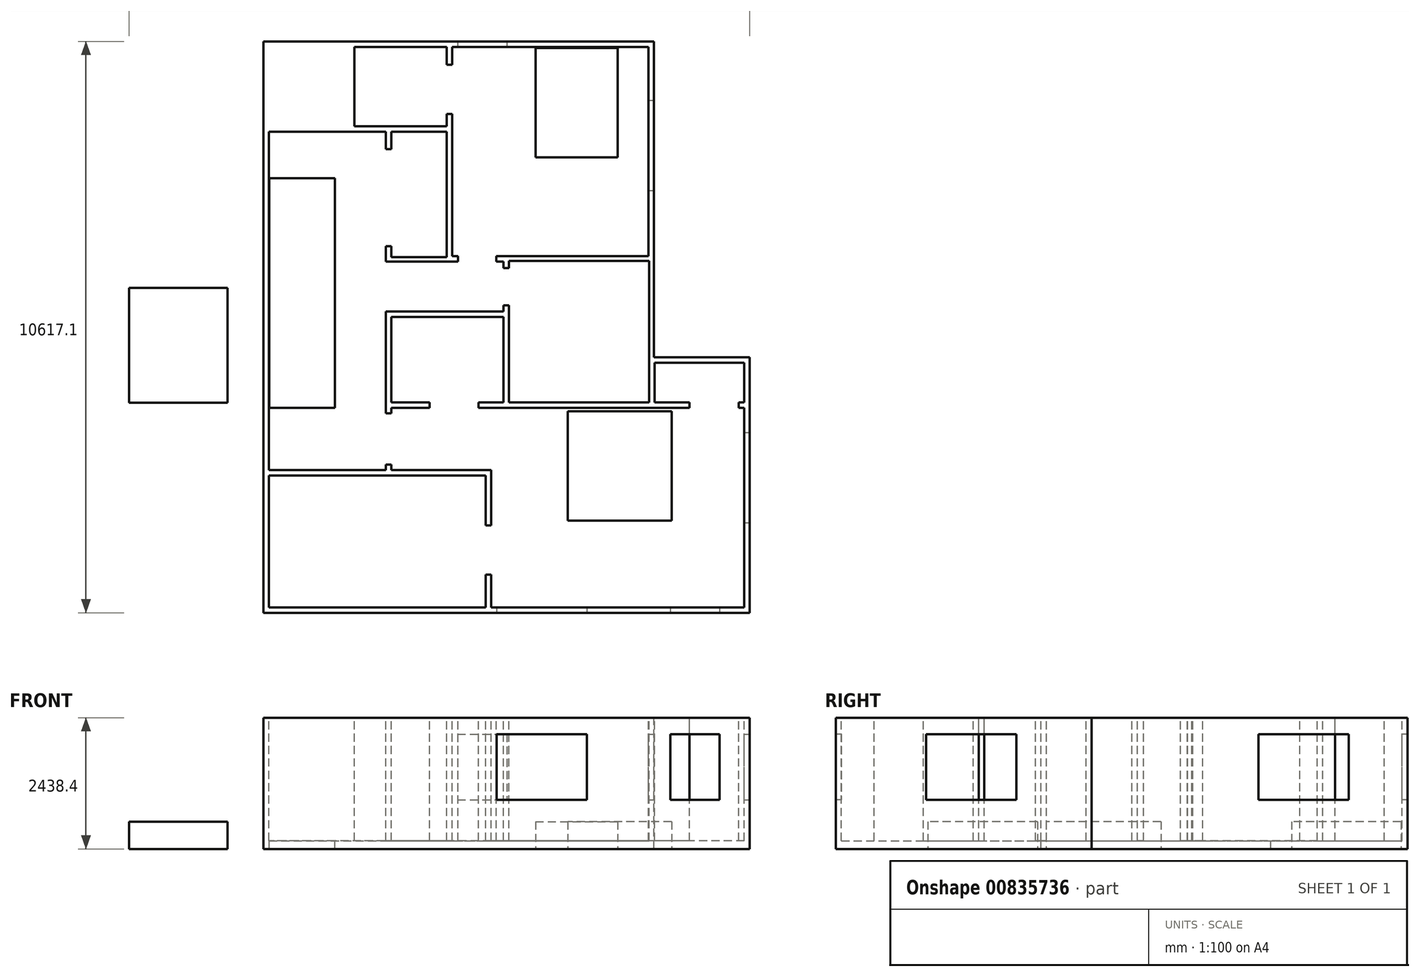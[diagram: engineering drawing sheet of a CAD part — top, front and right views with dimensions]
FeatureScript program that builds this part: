
annotation { "Feature Type Name" : "Feature", "Feature Type Description" : "" }
export const myFeature = defineFeature(function(context is Context, id is Id, definition is map)
    precondition{}
    {
        {
            var Q0;
            Q0=qCreatedBy(makeId("Top.planeOp"),FACE);
            var sketch = newSketch(context, id + "F0", { "sketchPlane" : qUnion([Q0])});
            skLineSegment(sketch, "E0.bottom", {"start": v(-4514.85, 5308.55) * mm, "end": v(4514.85, 5308.55) * mm});
            skLineSegment(sketch, "E0.top", {"start": v(-4514.85, -5308.55) * mm, "end": v(4514.85, -5308.55) * mm});
            skLineSegment(sketch, "E0.left", {"start": v(-4514.85, 5308.55) * mm, "end": v(-4514.85, -5308.55) * mm});
            skLineSegment(sketch, "E0.right", {"start": v(4514.85, 5308.55) * mm, "end": v(4514.85, -5308.55) * mm});
            skPoint(sketch, "E0.middle", {"position": v(0, 0) * mm});
            skSolve(sketch);
        }
        {
            var Q0;
            Q0 = qSketchRegion(id + "F0", true);
            extrude(context, id + "F1", {"entities" : qUnion([Q0]), "depth" : 2438.4 * mm, "offsetDistance" : 30.48 * mm});
        }
        {
            var Q0;
            Q0=makeQuery(id+"F1.opExtrude","CAP_FACE",FACE,{"disambiguationData":[OSD([sQuery(id+"F0.wireOp",EDGE,"E0.bottom"),sQuery(id+"F0.wireOp",EDGE,"E0.top"),sQuery(id+"F0.wireOp",EDGE,"E0.left"),sQuery(id+"F0.wireOp",EDGE,"E0.right")])],"isStart":false});
            var sketch = newSketch(context, id + "F2", { "sketchPlane" : qUnion([Q0])});
            skLineSegment(sketch, "E1.bottom", {"start": v(2736.95, 5308.55) * mm, "end": v(4514.85, 5308.55) * mm});
            skLineSegment(sketch, "E1.top", {"start": v(2736.95, -558.85) * mm, "end": v(4514.85, -558.85) * mm});
            skLineSegment(sketch, "E1.left", {"start": v(2736.95, 5308.55) * mm, "end": v(2736.95, -558.85) * mm});
            skLineSegment(sketch, "E1.right", {"start": v(4514.85, 5308.55) * mm, "end": v(4514.85, -558.85) * mm});
            skSolve(sketch);
        }
        {
            var Q0;
            Q0=makeQuery(id+"F2.imprint","IMPRINT",FACE,{"disambiguationData":[TD([[makeQuery(id+"F2.imprint","IMPRINT",EDGE,{"derivedFrom":sQuery(id+"F2.wireOp",EDGE,"E1.bottom")}),-1.0]])]});
            extrude(context, id + "F3", {"entities" : qUnion([Q0]), "operationType" : NewBodyOperationType.REMOVE, "oppositeDirection" : true, "depth" : 3048 * mm, "offsetDistance" : 30.48 * mm});
        }
        {
            var Q0;
            Q0=makeQuery(id+"F1.opExtrude","CAP_FACE",FACE,{"disambiguationData":[OSD([sQuery(id+"F0.wireOp",EDGE,"E0.bottom"),sQuery(id+"F0.wireOp",EDGE,"E0.top"),sQuery(id+"F0.wireOp",EDGE,"E0.left"),sQuery(id+"F0.wireOp",EDGE,"E0.right")])],"isStart":false});
            var sketch = newSketch(context, id + "F4", { "sketchPlane" : qUnion([Q0])});
            skLineSegment(sketch, "E2.bottom", {"start": v(4413.35, -5207.05) * mm, "end": v(-285.66, -5207.05) * mm});
            skLineSegment(sketch, "E2.top", {"start": v(4413.35, -1498.55) * mm, "end": v(4311.85, -1498.55) * mm});
            skLineSegment(sketch, "E2.left", {"start": v(4413.35, -5207.05) * mm, "end": v(4413.35, -3784.55) * mm});
            skLineSegment(sketch, "E2.right", {"start": v(-285.66, -5207.05) * mm, "end": v(-285.66, -4597.45) * mm});
            skLineSegment(sketch, "E3.bottom", {"start": v(-285.66, -1498.55) * mm, "end": v(-518.82, -1498.55) * mm});
            skLineSegment(sketch, "E3.right", {"start": v(-2144.32, -1498.55) * mm, "end": v(-2144.32, -1600.05) * mm});
            skLineSegment(sketch, "E4.bottom", {"start": v(-4413.35, -5207.05) * mm, "end": v(-387.16, -5207.05) * mm});
            skLineSegment(sketch, "E4.top", {"start": v(-4413.35, -2755.85) * mm, "end": v(-387.16, -2755.85) * mm});
            skLineSegment(sketch, "E4.left", {"start": v(-4413.35, -5207.05) * mm, "end": v(-4413.35, -2755.85) * mm});
            skLineSegment(sketch, "E4.right", {"start": v(-387.16, -5207.05) * mm, "end": v(-387.16, -4597.45) * mm});
            skLineSegment(sketch, "E5", {"start": v(-387.16, -4597.45) * mm, "end": v(-285.66, -4597.45) * mm});
            skLineSegment(sketch, "E6", {"start": v(-387.16, -3683.05) * mm, "end": v(-285.66, -3683.05) * mm});
            skLineSegment(sketch, "E7.trimOffspring", {"start": v(-387.16, -3683.05) * mm, "end": v(-387.16, -2755.85) * mm});
            skLineSegment(sketch, "E8.trimOffspring", {"start": v(4413.35, -2108.15) * mm, "end": v(4413.35, -1498.55) * mm});
            skLineSegment(sketch, "E9", {"start": v(4413.35, -3784.55) * mm, "end": v(4413.35, -2108.15) * mm});
            skLineSegment(sketch, "E10.bottom", {"start": v(-2144.32, -1397.05) * mm, "end": v(-1433.22, -1397.05) * mm});
            skLineSegment(sketch, "E10.top", {"start": v(-2144.32, 190.35) * mm, "end": v(-61.62, 190.35) * mm});
            skLineSegment(sketch, "E10.left", {"start": v(-2144.32, -1397.05) * mm, "end": v(-2144.32, 190.35) * mm});
            skLineSegment(sketch, "E10.right", {"start": v(-61.62, -1397.05) * mm, "end": v(-61.62, 190.35) * mm});
            skLineSegment(sketch, "E11.bottom", {"start": v(4413.35, -1397.05) * mm, "end": v(4311.85, -1397.05) * mm});
            skLineSegment(sketch, "E11.top", {"start": v(4413.35, -660.44) * mm, "end": v(2749.14, -660.44) * mm});
            skLineSegment(sketch, "E11.left", {"start": v(4413.35, -1397.05) * mm, "end": v(4413.35, -660.44) * mm});
            skLineSegment(sketch, "E11.right", {"start": v(2749.14, -1397.05) * mm, "end": v(2749.14, -660.44) * mm});
            skLineSegment(sketch, "E12", {"start": v(4311.85, -1397.05) * mm, "end": v(4311.85, -1498.55) * mm});
            skLineSegment(sketch, "E13", {"start": v(3397.45, -1397.05) * mm, "end": v(3397.45, -1498.55) * mm});
            skLineSegment(sketch, "E14.trimOffspring", {"start": v(3397.45, -1397.05) * mm, "end": v(2749.14, -1397.05) * mm});
            skLineSegment(sketch, "E15.trimOffspring", {"start": v(3397.45, -1498.55) * mm, "end": v(-285.66, -1498.55) * mm});
            skLineSegment(sketch, "E16", {"start": v(-518.82, -1397.05) * mm, "end": v(-518.82, -1498.55) * mm});
            skLineSegment(sketch, "E17", {"start": v(-1433.22, -1397.05) * mm, "end": v(-1433.22, -1498.55) * mm});
            skLineSegment(sketch, "E18.trimOffspring", {"start": v(-518.82, -1397.05) * mm, "end": v(-61.62, -1397.05) * mm});
            skLineSegment(sketch, "E19.trimOffspring", {"start": v(-1433.22, -1498.55) * mm, "end": v(-2144.32, -1498.55) * mm});
            skLineSegment(sketch, "E20.bottom", {"start": v(-2245.82, -2654.35) * mm, "end": v(-4413.35, -2654.35) * mm});
            skLineSegment(sketch, "E20.top", {"start": v(-2245.82, 3632.15) * mm, "end": v(-4413.35, 3632.15) * mm});
            skLineSegment(sketch, "E20.left", {"start": v(-2245.82, -2654.35) * mm, "end": v(-2245.82, -2552.85) * mm});
            skLineSegment(sketch, "E20.right", {"start": v(-4413.35, -2654.35) * mm, "end": v(-4413.35, 3632.15) * mm});
            skLineSegment(sketch, "E21", {"start": v(-285.66, -3683.05) * mm, "end": v(-285.66, -2654.35) * mm});
            skLineSegment(sketch, "E22", {"start": v(-285.66, -2654.35) * mm, "end": v(-2144.32, -2654.35) * mm});
            skLineSegment(sketch, "E23", {"start": v(-2245.82, -1600.05) * mm, "end": v(-2144.32, -1600.05) * mm});
            skLineSegment(sketch, "E24", {"start": v(-2144.32, -2552.85) * mm, "end": v(-2245.82, -2552.85) * mm});
            skLineSegment(sketch, "E25.trimOffspring", {"start": v(-2245.82, -1600.05) * mm, "end": v(-2245.82, 291.85) * mm});
            skLineSegment(sketch, "E26.trimOffspring", {"start": v(-2144.32, -2552.85) * mm, "end": v(-2144.32, -2654.35) * mm});
            skLineSegment(sketch, "E27.bottom", {"start": v(-2144.32, 3632.15) * mm, "end": v(-1114.6, 3632.15) * mm});
            skLineSegment(sketch, "E27.top", {"start": v(-2144.32, 1299.08) * mm, "end": v(-1114.6, 1299.08) * mm});
            skLineSegment(sketch, "E27.left", {"start": v(-2144.32, 3632.15) * mm, "end": v(-2144.32, 1299.08) * mm});
            skLineSegment(sketch, "E27.right", {"start": v(-1114.6, 3632.15) * mm, "end": v(-1114.6, 1299.08) * mm});
            skLineSegment(sketch, "E28", {"start": v(-2245.82, 3304.2) * mm, "end": v(-2144.32, 3304.2) * mm});
            skLineSegment(sketch, "E29", {"start": v(-2245.82, 1502.01) * mm, "end": v(-2144.32, 1502.01) * mm});
            skLineSegment(sketch, "E30.bottom", {"start": v(-2152.46, 1216.52) * mm, "end": v(-905.9, 1216.52) * mm});
            skLineSegment(sketch, "E30.top", {"start": v(-2152.46, 291.85) * mm, "end": v(-61.05, 291.85) * mm});
            skLineSegment(sketch, "E30.right", {"start": v(-61.05, 1216.52) * mm, "end": v(-61.05, 1093.18) * mm});
            skLineSegment(sketch, "E31.bottom", {"start": v(39.88, -1397.05) * mm, "end": v(2647.65, -1397.05) * mm});
            skLineSegment(sketch, "E31.top", {"start": v(39.88, 1226.25) * mm, "end": v(2647.65, 1226.25) * mm});
            skLineSegment(sketch, "E31.left", {"start": v(39.88, -1397.05) * mm, "end": v(39.88, 402.47) * mm});
            skLineSegment(sketch, "E31.right", {"start": v(2647.65, -1397.05) * mm, "end": v(2647.65, 1226.25) * mm});
            skLineSegment(sketch, "E32.bottom", {"start": v(-1013.1, 1318.02) * mm, "end": v(-905.9, 1318.02) * mm});
            skLineSegment(sketch, "E32.top", {"start": v(-1013.1, 5207.05) * mm, "end": v(2631.69, 5207.05) * mm});
            skLineSegment(sketch, "E32.left", {"start": v(-1013.1, 1318.02) * mm, "end": v(-1013.1, 3962.25) * mm});
            skLineSegment(sketch, "E32.right", {"start": v(2631.69, 1318.02) * mm, "end": v(2631.69, 5207.05) * mm});
            skLineSegment(sketch, "E33.bottom", {"start": v(-1114.6, 3733.65) * mm, "end": v(-2827.12, 3733.65) * mm});
            skLineSegment(sketch, "E33.top", {"start": v(-1114.6, 5207.05) * mm, "end": v(-2827.12, 5207.05) * mm});
            skLineSegment(sketch, "E33.left", {"start": v(-1114.6, 3733.65) * mm, "end": v(-1114.6, 3962.25) * mm});
            skLineSegment(sketch, "E33.right", {"start": v(-2827.12, 3733.65) * mm, "end": v(-2827.12, 5207.05) * mm});
            skLineSegment(sketch, "E34", {"start": v(-1114.6, 3962.25) * mm, "end": v(-1013.1, 3962.25) * mm});
            skLineSegment(sketch, "E35", {"start": v(-1114.6, 4876.65) * mm, "end": v(-1013.1, 4876.65) * mm});
            skLineSegment(sketch, "E36.trimOffspring", {"start": v(-1114.6, 4876.65) * mm, "end": v(-1114.6, 5207.05) * mm});
            skLineSegment(sketch, "E37.trimOffspring", {"start": v(-1013.1, 4876.65) * mm, "end": v(-1013.1, 5207.05) * mm});
            skLineSegment(sketch, "E38", {"start": v(-2152.46, 291.85) * mm, "end": v(-2245.82, 291.85) * mm});
            skLineSegment(sketch, "E39", {"start": v(-2152.46, 1216.52) * mm, "end": v(-2245.82, 1216.52) * mm});
            skLineSegment(sketch, "E40.trimOffspring", {"start": v(-2245.82, 1216.52) * mm, "end": v(-2245.82, 3632.15) * mm});
            skLineSegment(sketch, "E41", {"start": v(-905.9, 1318.02) * mm, "end": v(-905.9, 1216.52) * mm});
            skLineSegment(sketch, "E42", {"start": v(-189.14, 1318.02) * mm, "end": v(-189.14, 1216.52) * mm});
            skLineSegment(sketch, "E43", {"start": v(-61.05, 1093.18) * mm, "end": v(39.88, 1093.18) * mm});
            skLineSegment(sketch, "E44", {"start": v(-61.05, 402.47) * mm, "end": v(39.88, 402.47) * mm});
            skLineSegment(sketch, "E45.trimOffspring", {"start": v(-189.14, 1318.02) * mm, "end": v(2631.69, 1318.02) * mm});
            skLineSegment(sketch, "E46.trimOffspring", {"start": v(-189.14, 1216.52) * mm, "end": v(-61.05, 1216.52) * mm});
            skLineSegment(sketch, "E47.trimOffspring", {"start": v(-61.05, 402.47) * mm, "end": v(-61.05, 291.85) * mm});
            skLineSegment(sketch, "E48.trimOffspring", {"start": v(39.88, 1093.18) * mm, "end": v(39.88, 1226.25) * mm});
            skSolve(sketch);
        }
        {
            var Q0;
            Q0 = qSketchRegion(id + "F4", true);
            extrude(context, id + "F5", {"entities" : qUnion([Q0]), "operationType" : NewBodyOperationType.REMOVE, "oppositeDirection" : true, "depth" : 2286 * mm, "offsetDistance" : 30.48 * mm});
        }
        {
            var Q0;
            Q0=qCreatedBy(makeId("Top.planeOp"),FACE);
            cPlane(context, id + "F6", {"entities" : qUnion([Q0]), "cplaneType" : CPlaneType.OFFSET, "offset" : 914.4 * mm, "width" : 152.4 * mm, "height" : 152.4 * mm});
        }
        {
            var Q0;
            Q0=qCreatedBy(id+"F6.planeOp",FACE);
            var sketch = newSketch(context, id + "F7", { "sketchPlane" : qUnion([Q0])});
            skLineSegment(sketch, "E49.bottom", {"start": v(4335.38, -1955.75) * mm, "end": v(4679.64, -1955.75) * mm});
            skLineSegment(sketch, "E49.top", {"start": v(4335.38, -3632.15) * mm, "end": v(4679.64, -3632.15) * mm});
            skLineSegment(sketch, "E49.left", {"start": v(4335.38, -1955.75) * mm, "end": v(4335.38, -3632.15) * mm});
            skLineSegment(sketch, "E49.right", {"start": v(4679.64, -1955.75) * mm, "end": v(4679.64, -3632.15) * mm});
            skLineSegment(sketch, "E50.bottom", {"start": v(-184.16, -5015.75) * mm, "end": v(1492.24, -5015.75) * mm});
            skLineSegment(sketch, "E50.top", {"start": v(-184.16, -5465.66) * mm, "end": v(1492.24, -5465.66) * mm});
            skLineSegment(sketch, "E50.left", {"start": v(-184.16, -5015.75) * mm, "end": v(-184.16, -5465.66) * mm});
            skLineSegment(sketch, "E50.right", {"start": v(1492.24, -5015.75) * mm, "end": v(1492.24, -5465.66) * mm});
            skLineSegment(sketch, "E51.bottom", {"start": v(3041.75, -5049.07) * mm, "end": v(3956.15, -5049.07) * mm});
            skLineSegment(sketch, "E51.top", {"start": v(3041.75, -5465.66) * mm, "end": v(3956.15, -5465.66) * mm});
            skLineSegment(sketch, "E51.left", {"start": v(3041.75, -5049.07) * mm, "end": v(3041.75, -5465.66) * mm});
            skLineSegment(sketch, "E51.right", {"start": v(3956.15, -5049.07) * mm, "end": v(3956.15, -5465.66) * mm});
            skLineSegment(sketch, "E52.bottom", {"start": v(2559.45, 4213.62) * mm, "end": v(2959.38, 4213.62) * mm});
            skLineSegment(sketch, "E52.top", {"start": v(2559.45, 2537.22) * mm, "end": v(2959.38, 2537.22) * mm});
            skLineSegment(sketch, "E52.left", {"start": v(2559.45, 4213.62) * mm, "end": v(2559.45, 2537.22) * mm});
            skLineSegment(sketch, "E52.right", {"start": v(2959.38, 4213.62) * mm, "end": v(2959.38, 2537.22) * mm});
            skLineSegment(sketch, "E53.bottom", {"start": v(-911.61, 5499) * mm, "end": v(2.79, 5499) * mm});
            skLineSegment(sketch, "E53.top", {"start": v(-911.61, 4932.43) * mm, "end": v(2.79, 4932.43) * mm});
            skLineSegment(sketch, "E53.left", {"start": v(-911.61, 5499) * mm, "end": v(-911.61, 4932.43) * mm});
            skLineSegment(sketch, "E53.right", {"start": v(2.79, 5499) * mm, "end": v(2.79, 4932.43) * mm});
            skSolve(sketch);
        }
        {
            var Q0;
            Q0 = qSketchRegion(id + "F7", true);
            extrude(context, id + "F8", {"entities" : qUnion([Q0]), "operationType" : NewBodyOperationType.REMOVE, "depth" : 1219.2 * mm, "offsetDistance" : 30.48 * mm});
        }
        {
            var Q0;
            Q0=makeQuery(id+"F5.boolean.opBoolean","COPY",FACE,{"derivedFrom":makeQuery(id+"F5.opExtrude","CAP_FACE",FACE,{"disambiguationData":[OSD([sQuery(id+"F4.wireOp",EDGE,"E2.bottom"),sQuery(id+"F4.wireOp",EDGE,"E2.top"),sQuery(id+"F4.wireOp",EDGE,"E2.left"),sQuery(id+"F4.wireOp",EDGE,"E2.right"),sQuery(id+"F4.wireOp",EDGE,"E3.bottom"),sQuery(id+"F4.wireOp",EDGE,"E3.right"),sQuery(id+"F4.wireOp",EDGE,"E4.bottom"),sQuery(id+"F4.wireOp",EDGE,"E4.top"),sQuery(id+"F4.wireOp",EDGE,"E4.left"),sQuery(id+"F4.wireOp",EDGE,"E4.right"),sQuery(id+"F4.wireOp",EDGE,"E5"),sQuery(id+"F4.wireOp",EDGE,"E6"),sQuery(id+"F4.wireOp",EDGE,"E7.trimOffspring"),sQuery(id+"F4.wireOp",EDGE,"E8.trimOffspring"),sQuery(id+"F4.wireOp",EDGE,"E9"),sQuery(id+"F4.wireOp",EDGE,"E10.bottom"),sQuery(id+"F4.wireOp",EDGE,"E10.top"),sQuery(id+"F4.wireOp",EDGE,"E10.left"),sQuery(id+"F4.wireOp",EDGE,"E10.right"),sQuery(id+"F4.wireOp",EDGE,"E11.bottom"),sQuery(id+"F4.wireOp",EDGE,"E11.top"),sQuery(id+"F4.wireOp",EDGE,"E11.left"),sQuery(id+"F4.wireOp",EDGE,"E11.right"),sQuery(id+"F4.wireOp",EDGE,"E12"),sQuery(id+"F4.wireOp",EDGE,"E13"),sQuery(id+"F4.wireOp",EDGE,"E14.trimOffspring"),sQuery(id+"F4.wireOp",EDGE,"E15.trimOffspring"),sQuery(id+"F4.wireOp",EDGE,"E16"),sQuery(id+"F4.wireOp",EDGE,"E17"),sQuery(id+"F4.wireOp",EDGE,"E18.trimOffspring"),sQuery(id+"F4.wireOp",EDGE,"E19.trimOffspring"),sQuery(id+"F4.wireOp",EDGE,"E20.bottom"),sQuery(id+"F4.wireOp",EDGE,"E20.top"),sQuery(id+"F4.wireOp",EDGE,"E20.left"),sQuery(id+"F4.wireOp",EDGE,"E20.right"),sQuery(id+"F4.wireOp",EDGE,"E21"),sQuery(id+"F4.wireOp",EDGE,"E22"),sQuery(id+"F4.wireOp",EDGE,"E23"),sQuery(id+"F4.wireOp",EDGE,"E24"),sQuery(id+"F4.wireOp",EDGE,"E25.trimOffspring"),sQuery(id+"F4.wireOp",EDGE,"E26.trimOffspring"),sQuery(id+"F4.wireOp",EDGE,"E27.bottom"),sQuery(id+"F4.wireOp",EDGE,"E27.top"),sQuery(id+"F4.wireOp",EDGE,"E27.left"),sQuery(id+"F4.wireOp",EDGE,"E27.right"),sQuery(id+"F4.wireOp",EDGE,"E28"),sQuery(id+"F4.wireOp",EDGE,"E29"),sQuery(id+"F4.wireOp",EDGE,"E30.bottom"),sQuery(id+"F4.wireOp",EDGE,"E30.top"),sQuery(id+"F4.wireOp",EDGE,"E30.right"),sQuery(id+"F4.wireOp",EDGE,"E31.bottom"),sQuery(id+"F4.wireOp",EDGE,"E31.top"),sQuery(id+"F4.wireOp",EDGE,"E31.left"),sQuery(id+"F4.wireOp",EDGE,"E31.right"),sQuery(id+"F4.wireOp",EDGE,"E32.bottom"),sQuery(id+"F4.wireOp",EDGE,"E32.top"),sQuery(id+"F4.wireOp",EDGE,"E32.left"),sQuery(id+"F4.wireOp",EDGE,"E32.right"),sQuery(id+"F4.wireOp",EDGE,"E33.bottom"),sQuery(id+"F4.wireOp",EDGE,"E33.top"),sQuery(id+"F4.wireOp",EDGE,"E33.left"),sQuery(id+"F4.wireOp",EDGE,"E33.right"),sQuery(id+"F4.wireOp",EDGE,"E34"),sQuery(id+"F4.wireOp",EDGE,"E35"),sQuery(id+"F4.wireOp",EDGE,"E36.trimOffspring"),sQuery(id+"F4.wireOp",EDGE,"E37.trimOffspring"),sQuery(id+"F4.wireOp",EDGE,"E38"),sQuery(id+"F4.wireOp",EDGE,"E39"),sQuery(id+"F4.wireOp",EDGE,"E40.trimOffspring"),sQuery(id+"F4.wireOp",EDGE,"E41"),sQuery(id+"F4.wireOp",EDGE,"E42"),sQuery(id+"F4.wireOp",EDGE,"E43"),sQuery(id+"F4.wireOp",EDGE,"E44"),sQuery(id+"F4.wireOp",EDGE,"E45.trimOffspring"),sQuery(id+"F4.wireOp",EDGE,"E46.trimOffspring"),sQuery(id+"F4.wireOp",EDGE,"E47.trimOffspring"),sQuery(id+"F4.wireOp",EDGE,"E48.trimOffspring")])],"isStart":false})});
            var sketch = newSketch(context, id + "F9", { "sketchPlane" : qUnion([Q0])});
            skLineSegment(sketch, "E54.bottom", {"start": v(-3190.31, -1498.55) * mm, "end": v(-4409.51, -1498.55) * mm});
            skLineSegment(sketch, "E54.top", {"start": v(-3190.31, 2768.65) * mm, "end": v(-4409.51, 2768.65) * mm});
            skLineSegment(sketch, "E54.left", {"start": v(-3190.31, -1498.55) * mm, "end": v(-3190.31, 2768.65) * mm});
            skLineSegment(sketch, "E54.right", {"start": v(-4409.51, -1498.55) * mm, "end": v(-4409.51, 2768.65) * mm});
            skSolve(sketch);
        }
        {
            var Q0;
            Q0=makeQuery(id+"F9.imprint","IMPRINT",FACE,{"disambiguationData":[TD([[makeQuery(id+"F9.imprint","IMPRINT",EDGE,{"derivedFrom":sQuery(id+"F9.wireOp",EDGE,"E54.bottom")}),-1.0]])]});
            extrude(context, id + "F10", {"entities" : qUnion([Q0]), "operationType" : NewBodyOperationType.REMOVE, "oppositeDirection" : true, "depth" : 1524 * mm, "offsetDistance" : 30.48 * mm});
        }
        {
            var Q0;
            Q0=qCreatedBy(makeId("Top.planeOp"),FACE);
            var sketch = newSketch(context, id + "F11", { "sketchPlane" : qUnion([Q0])});
            skLineSegment(sketch, "E55.bottom", {"start": v(535.8, 5184.42) * mm, "end": v(2059.8, 5184.42) * mm});
            skLineSegment(sketch, "E55.top", {"start": v(535.8, 3152.42) * mm, "end": v(2059.8, 3152.42) * mm});
            skLineSegment(sketch, "E55.left", {"start": v(535.8, 5184.42) * mm, "end": v(535.8, 3152.42) * mm});
            skLineSegment(sketch, "E55.right", {"start": v(2059.8, 5184.42) * mm, "end": v(2059.8, 3152.42) * mm});
            skSolve(sketch);
        }
        {
            var Q0;
            Q0=makeQuery(id+"F11.imprint","IMPRINT",FACE,{"disambiguationData":[TD([[makeQuery(id+"F11.imprint","IMPRINT",EDGE,{"derivedFrom":sQuery(id+"F11.wireOp",EDGE,"E55.bottom")}),-1.0]])]});
            extrude(context, id + "F12", {"entities" : qUnion([Q0]), "depth" : 508 * mm, "offsetDistance" : 30.48 * mm});
        }
        {
            var Q0;
            Q0=qCreatedBy(makeId("Top.planeOp"),FACE);
            var sketch = newSketch(context, id + "F13", { "sketchPlane" : qUnion([Q0])});
            skLineSegment(sketch, "E56.bottom", {"start": v(3063.5, -1566.38) * mm, "end": v(1133.1, -1566.38) * mm});
            skLineSegment(sketch, "E56.top", {"start": v(3063.5, -3598.38) * mm, "end": v(1133.1, -3598.38) * mm});
            skLineSegment(sketch, "E56.left", {"start": v(3063.5, -1566.38) * mm, "end": v(3063.5, -3598.38) * mm});
            skLineSegment(sketch, "E56.right", {"start": v(1133.1, -1566.38) * mm, "end": v(1133.1, -3598.38) * mm});
            skSolve(sketch);
        }
        {
            var Q0;
            Q0 = qSketchRegion(id + "F13", true);
            extrude(context, id + "F14", {"entities" : qUnion([Q0]), "depth" : 508 * mm, "offsetDistance" : 30.48 * mm});
        }
        {
            var Q0;
            Q0=qCreatedBy(makeId("Top.planeOp"),FACE);
            var sketch = newSketch(context, id + "F15", { "sketchPlane" : qUnion([Q0])});
            skLineSegment(sketch, "E57.bottom", {"start": v(-7010.27, 729.82) * mm, "end": v(-5181.47, 729.82) * mm});
            skLineSegment(sketch, "E57.top", {"start": v(-7010.27, -1403.78) * mm, "end": v(-5181.47, -1403.78) * mm});
            skLineSegment(sketch, "E57.left", {"start": v(-7010.27, 729.82) * mm, "end": v(-7010.27, -1403.78) * mm});
            skLineSegment(sketch, "E57.right", {"start": v(-5181.47, 729.82) * mm, "end": v(-5181.47, -1403.78) * mm});
            skSolve(sketch);
        }
        {
            var Q0;
            Q0=makeQuery(id+"F15.imprint","IMPRINT",FACE,{"disambiguationData":[TD([[makeQuery(id+"F15.imprint","IMPRINT",EDGE,{"derivedFrom":sQuery(id+"F15.wireOp",EDGE,"E57.bottom")}),-1.0]])]});
            extrude(context, id + "F16", {"entities" : qUnion([Q0]), "depth" : 508 * mm, "offsetDistance" : 30.48 * mm});
        }
    });
